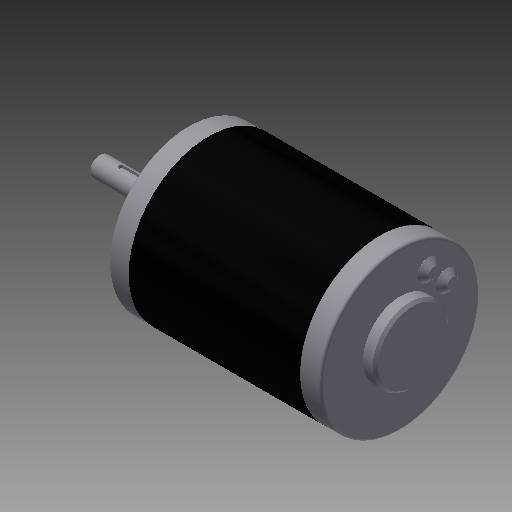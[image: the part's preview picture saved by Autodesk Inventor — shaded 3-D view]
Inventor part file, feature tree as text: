
AUTODESK INVENTOR PART (.ipt)
format: ipt  version: 2017 (Build 210142000, 142)  size: 176,640 bytes
history: native  units: in
note: dims shown in document units (in); Inventor stores cm internally (conversion verified against a paired STEP export)
features: chamfer x1, other x1, imported_body x1
ambient origin geometry x8: Origin, YZ Plane, XZ Plane, XY Plane, X Axis, Y Axis, Z Axis, Center Point
bodies: Body1 (feature_tree)
feature tree (3):
  chamfer  "Chamfer3"  [1 undecoded]
  other  "Mini CIM Motor1"
  imported_body  "Base1"
note: 1 required parameter value undecoded (feature->parameter linkage not recoverable at this tier; creation-order binding heuristic only, values carry confidence <= 0.55)
